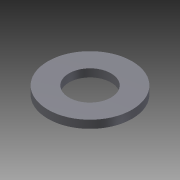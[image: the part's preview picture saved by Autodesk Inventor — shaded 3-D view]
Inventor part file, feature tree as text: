
AUTODESK INVENTOR PART (.ipt)
format: ipt  version: 2012 (Build 160160000, 160)  size: 73,216 bytes
history: native  units: mm
features: extrude x1, sketch x1
ambient origin geometry x8: Origin, YZ Plane, XZ Plane, XY Plane, X Axis, Y Axis, Z Axis, Center Point
bodies: Solid1 (feature_tree)
feature tree (2):
  extrude  "Extrusion1"  Depth=16.0mm
  sketch  "Sketch1"  dims[d0=8.0mm d1=16.0mm d2=1.5mm d3=0.0mm]
